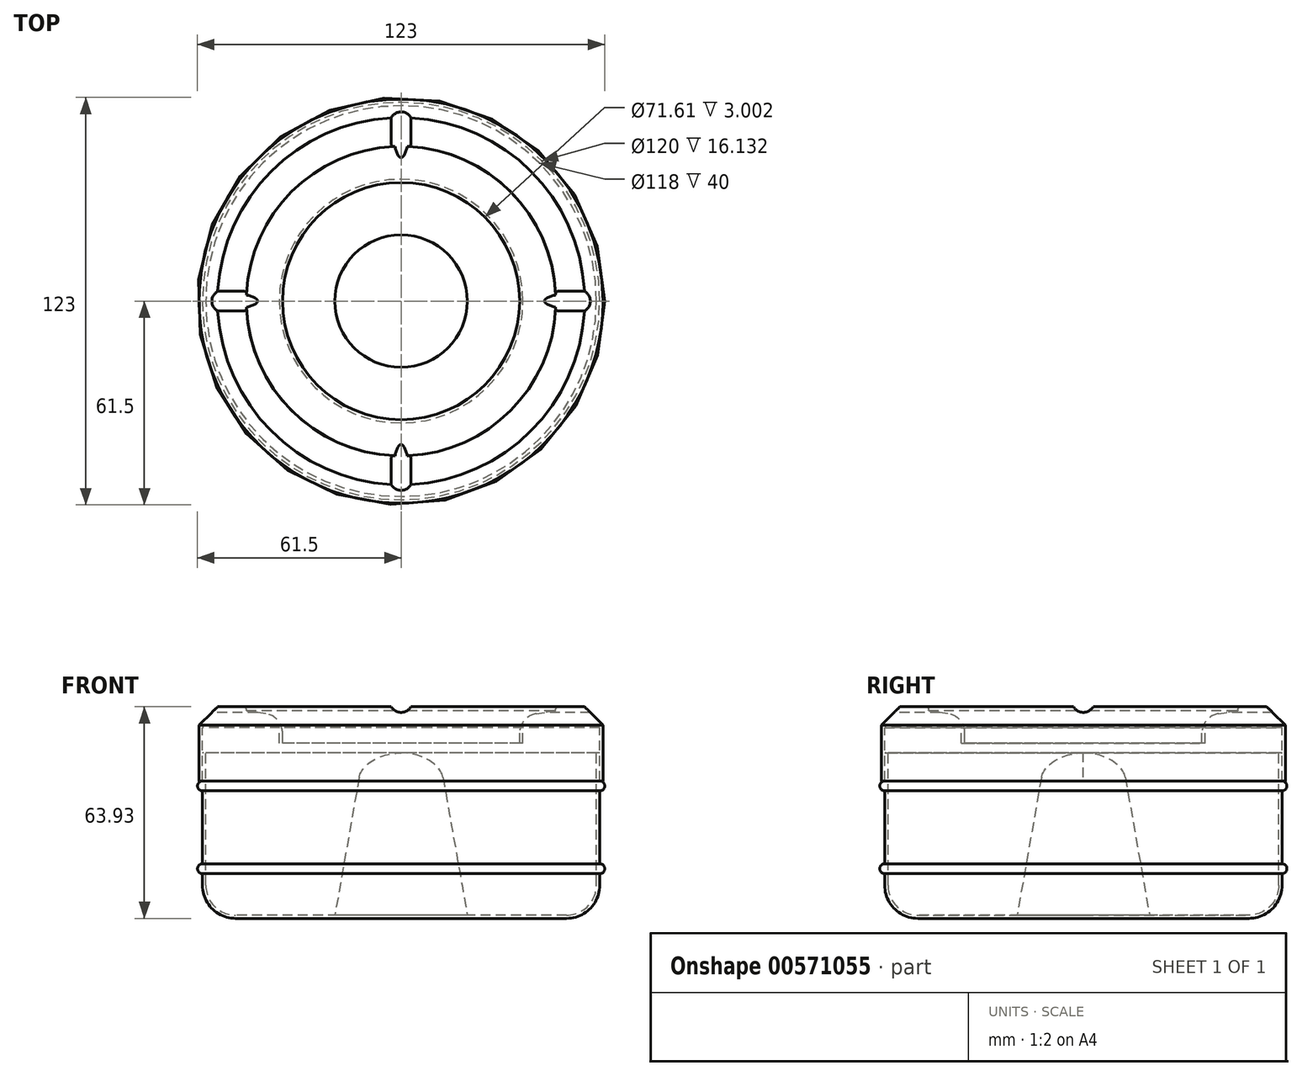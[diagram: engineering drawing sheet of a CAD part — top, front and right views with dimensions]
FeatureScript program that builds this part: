
annotation { "Feature Type Name" : "Feature", "Feature Type Description" : "" }
export const myFeature = defineFeature(function(context is Context, id is Id, definition is map)
    precondition{}
    {
        {
            var Q0;
            Q0=qCreatedBy(makeId("Front.planeOp"),FACE);
            var sketch = newSketch(context, id + "F0", { "sketchPlane" : qUnion([Q0])});
            skLineSegment(sketch, "E0", {"start": v(-12.67, 42.6) * mm, "end": v(-20, 1) * mm});
            skLineSegment(sketch, "E1", {"start": v(-20, 1) * mm, "end": v(-50, 1) * mm});
            skLineSegment(sketch, "E2", {"start": v(-59, 10) * mm, "end": v(-59, 50) * mm});
            skLineSegment(sketch, "E3", {"start": v(0, 50) * mm, "end": v(0, 0) * mm});
            skLineSegment(sketch, "E4", {"start": v(0, 0) * mm, "end": v(-50, 0) * mm});
            skLineSegment(sketch, "E5", {"start": v(-60, 10) * mm, "end": v(-60, 13.5) * mm});
            skLineSegment(sketch, "E6", {"start": v(-60, 13.5) * mm, "end": v(-60, 13.5) * mm});
            skLineSegment(sketch, "E7", {"start": v(-59, 50) * mm, "end": v(-60, 50) * mm});
            skLineSegment(sketch, "E8", {"start": v(-60, 50) * mm, "end": v(-60, 41.5) * mm});
            skLineSegment(sketch, "E9", {"start": v(-60, 41.5) * mm, "end": v(-60, 41.5) * mm});
            skLineSegment(sketch, "E10", {"start": v(0, 42.62) * mm, "end": v(0, -34.97) * mm, "construction": true});
            skLineSegment(sketch, "E11", {"start": v(-60, 13.5) * mm, "end": v(-60, 69.5) * mm, "construction": true});
            skArc(sketch, "E12", {"start": v(-60, 16.5) * mm, "mid": v(-61.5, 15) * mm, "end": v(-60, 13.5) * mm});
            skArc(sketch, "E13", {"start": v(-60, 41.5) * mm, "mid": v(-61.5, 40) * mm, "end": v(-60, 38.5) * mm});
            skLineSegment(sketch, "E14", {"start": v(-60, 16.5) * mm, "end": v(-60, 38.5) * mm});
            skPoint(sketch, "E15.visualSharp", {"position": v(-60, 0) * mm});
            skArc(sketch, "E15.filletArc", {"start": v(-60, 10) * mm, "mid": v(-57.07, 2.93) * mm, "end": v(-50, 0) * mm});
            skPoint(sketch, "E16.visualSharp", {"position": v(-59, 1) * mm});
            skArc(sketch, "E16.filletArc", {"start": v(-59, 10) * mm, "mid": v(-56.36, 3.64) * mm, "end": v(-50, 1) * mm});
            skPoint(sketch, "E17.visualSharp", {"position": v(-10, 57.7) * mm});
            skFitSpline(sketch, "E18", {"points": [v(-12.67, 42.6) * mm, v(0, 50) * mm], "startDerivative": vector(2.05, 11.61) * mm, "endDerivative": vector(18.84, 0) * mm});
            skSolve(sketch);
        }
        {
            var Q0;
            Q0=makeQuery(id+"F0.imprint","IMPRINT",FACE,{"disambiguationData":[TD([[makeQuery(id+"F0.imprint","IMPRINT",EDGE,{"derivedFrom":sQuery(id+"F0.wireOp",EDGE,"216fbe1d-88b9-4d87-ae66-dd3ea7f10c52")}),1.0]])]});
            var Q1;
            Q1=makeQuery(id+"F0.imprint","IMPRINT",FACE,{"disambiguationData":[TD([[makeQuery(id+"F0.imprint","IMPRINT",EDGE,{"derivedFrom":sQuery(id+"F0.wireOp",EDGE,"E0")}),1.0]])]});
            var Q2;
            Q2=sQuery(id+"F0.wireOp",EDGE,"E10");
            revolve(context, id + "F1", {"entities" : qUnion([Q0, Q1]), "axis" : qUnion([Q2]), "revolveType" : RevolveType.FULL});
        }
        {
            var Q0;
            Q0=qCreatedBy(makeId("Front.planeOp"),FACE);
            var sketch = newSketch(context, id + "F2", { "sketchPlane" : qUnion([Q0])});
            skLineSegment(sketch, "E19", {"start": v(0, 127.4) * mm, "end": v(0, 57.1) * mm, "construction": true});
            skLineSegment(sketch, "E20.0", {"start": v(-60, 41.5) * mm, "end": v(60, 41.5) * mm, "construction": true});
            skLineSegment(sketch, "E21", {"start": v(-60, 41.5) * mm, "end": v(-60, 57.63) * mm});
            skLineSegment(sketch, "E22", {"start": v(-60, 41.5) * mm, "end": v(-61, 41.5) * mm});
            skLineSegment(sketch, "E23", {"start": v(-61, 41.5) * mm, "end": v(-61, 58.4) * mm});
            skLineSegment(sketch, "E24", {"start": v(-61, 58.4) * mm, "end": v(-55.46, 63.93) * mm});
            skLineSegment(sketch, "E25", {"start": v(-55.46, 63.93) * mm, "end": v(-46.76, 63.93) * mm});
            skLineSegment(sketch, "E26", {"start": v(-46.76, 63.93) * mm, "end": v(-46.76, 63.93) * mm});
            skLineSegment(sketch, "E27", {"start": v(-36.8, 52.92) * mm, "end": v(-35.8, 52.92) * mm});
            skLineSegment(sketch, "E28", {"start": v(-60, 57.63) * mm, "end": v(-36.8, 57.63) * mm});
            skLineSegment(sketch, "E29", {"start": v(-36.8, 57.63) * mm, "end": v(-36.8, 52.92) * mm});
            skLineSegment(sketch, "E30", {"start": v(-46.76, 62.77) * mm, "end": v(-35.8, 61.06) * mm});
            skLineSegment(sketch, "E31", {"start": v(-35.8, 61.06) * mm, "end": v(-35.8, 52.92) * mm});
            skLineSegment(sketch, "E32", {"start": v(-46.76, 63.93) * mm, "end": v(-46.76, 62.77) * mm});
            skSolve(sketch);
        }
        {
            var Q0;
            Q0=makeQuery(id+"F2.imprint","IMPRINT",FACE,{"disambiguationData":[TD([[makeQuery(id+"F2.imprint","IMPRINT",EDGE,{"derivedFrom":sQuery(id+"F2.wireOp",EDGE,"0ef7d9b7-cdab-4da3-8be8-f22e8d8c60c7")}),1.0]])]});
            var Q1;
            Q1=makeQuery(id+"F2.imprint","IMPRINT",FACE,{"disambiguationData":[TD([[makeQuery(id+"F2.imprint","IMPRINT",EDGE,{"derivedFrom":sQuery(id+"F2.wireOp",EDGE,"E21")}),1.0]])]});
            var Q2;
            Q2=sQuery(id+"F2.wireOp",EDGE,"0ef7d9b7-cdab-4da3-8be8-f22e8d8c60c7");
            var Q3;
            Q3=sQuery(id+"F2.wireOp",EDGE,"aa0ec3b9-b7ba-45df-8467-560e599c3e96");
            var Q4;
            Q4=sQuery(id+"F2.wireOp",EDGE,"3610fc54-81f4-475f-afcd-191f41fe90ad");
            var Q5;
            Q5=sQuery(id+"F2.wireOp",EDGE,"8da40159-667a-4818-8d4f-36d4c085a2f0");
            var Q6;
            Q6=sQuery(id+"F2.wireOp",EDGE,"1ba69f26-8105-4ef7-89f6-a7fc1c6d1f82");
            var Q7;
            Q7=sQuery(id+"F2.wireOp",EDGE,"E19");
            revolve(context, id + "F3", {"entities" : qUnion([Q0, Q1]), "surfaceEntities" : qUnion([Q2, Q3, Q4, Q5, Q6]), "axis" : qUnion([Q7]), "revolveType" : RevolveType.FULL});
        }
        {
            var Q0;
            Q0=qCreatedBy(makeId("Front.planeOp"),FACE);
            var sketch = newSketch(context, id + "F4", { "sketchPlane" : qUnion([Q0])});
            skLineSegment(sketch, "E33.0", {"start": v(-55.46, 63.93) * mm, "end": v(55.46, 63.93) * mm, "construction": true});
            skLineSegment(sketch, "E34", {"start": v(-3, 63.93) * mm, "end": v(3, 63.93) * mm});
            skArc(sketch, "E35", {"start": v(3, 63.93) * mm, "mid": v(0, 62.23) * mm, "end": v(-3, 63.93) * mm});
            skPoint(sketch, "E35.centerSnap0", {"position": v(0, 63.93) * mm});
            skSolve(sketch);
        }
        {
            var Q0;
            Q0=makeQuery(id+"F3.opRevolve","SWEPT_EDGE",EDGE,{"disambiguationData":[OSD([sQuery(id+"F2.wireOp",EDGE,"E30"),sQuery(id+"F2.wireOp",EDGE,"E31")])]});
            fillet(context, id + "F5", {"entities" : qUnion([Q0]), "radius" : 6 * mm, "tangentPropagation" : true, "allowEdgeOverflow" : false});
        }
        {
            var Q0;
            {var subQ0=sQuery(id+"F2.wireOp",EDGE,"E25");var subQ1=sQuery(id+"F2.wireOp",EDGE,"E32");Q0=makeQuery(id+"F9.boolean.opBoolean","SPLIT",EDGE,{"disambiguationData":[TD([makeQuery(id+"F7.boolean.opBoolean","COPY",FACE,{"disambiguationData":[OD(1.0)],"derivedFrom":makeQuery(id+"F7.opExtrude","SWEPT_FACE",FACE,{"disambiguationData":[OSD([sQuery(id+"F4.wireOp",EDGE,"E35")])]})})])],"derivedFrom":makeQuery(id+"F7.boolean.opBoolean","SPLIT",EDGE,{"disambiguationData":[OD(0.0)],"derivedFrom":makeQuery(id+"F3.opRevolve","SWEPT_EDGE",EDGE,{"disambiguationData":[OSD([subQ0,subQ1])]})})});}
            fillet(context, id + "F6", {"entities" : qUnion([Q0]), "radius" : 1 * mm, "tangentPropagation" : true, "allowEdgeOverflow" : false});
        }
        {
            var Q0;
            Q0=makeQuery(id+"F4.imprint","IMPRINT",FACE,{"disambiguationData":[TD([[makeQuery(id+"F4.imprint","IMPRINT",EDGE,{"derivedFrom":sQuery(id+"F4.wireOp",EDGE,"E34")}),-1.0]])]});
            extrude(context, id + "F7", {"entities" : qUnion([Q0]), "operationType" : NewBodyOperationType.REMOVE, "endBound" : BoundingType.THROUGH_ALL, "oppositeDirection" : true, "depth" : 25 * mm, "offsetDistance" : 25 * mm, "hasSecondDirection" : true, "secondDirectionBound" : SecondDirectionBoundingType.THROUGH_ALL, "secondDirectionOppositeDirection" : false, "secondDirectionDepth" : 25 * mm});
        }
        {
            var Q0;
            Q0=qCreatedBy(makeId("Right.planeOp"),FACE);
            var sketch = newSketch(context, id + "F8", { "sketchPlane" : qUnion([Q0])});
            skLineSegment(sketch, "E36.0", {"start": v(55.38, 63.93) * mm, "end": v(-55.38, 63.93) * mm, "construction": true});
            skLineSegment(sketch, "E37", {"start": v(3, 63.93) * mm, "end": v(-3, 63.93) * mm});
            skArc(sketch, "E38", {"start": v(-3, 63.93) * mm, "mid": v(0, 62.23) * mm, "end": v(3, 63.93) * mm});
            skPoint(sketch, "E38.centerSnap0", {"position": v(0, 63.93) * mm});
            skSolve(sketch);
        }
        {
            var Q0;
            Q0=makeQuery(id+"F8.imprint","IMPRINT",FACE,{"disambiguationData":[TD([[makeQuery(id+"F8.imprint","IMPRINT",EDGE,{"derivedFrom":sQuery(id+"F8.wireOp",EDGE,"E37")}),1.0]])]});
            extrude(context, id + "F9", {"entities" : qUnion([Q0]), "operationType" : NewBodyOperationType.REMOVE, "endBound" : BoundingType.THROUGH_ALL, "depth" : 25 * mm, "offsetDistance" : 25 * mm, "hasSecondDirection" : true, "secondDirectionBound" : SecondDirectionBoundingType.THROUGH_ALL, "secondDirectionOppositeDirection" : true, "secondDirectionDepth" : 25 * mm});
        }
    });
